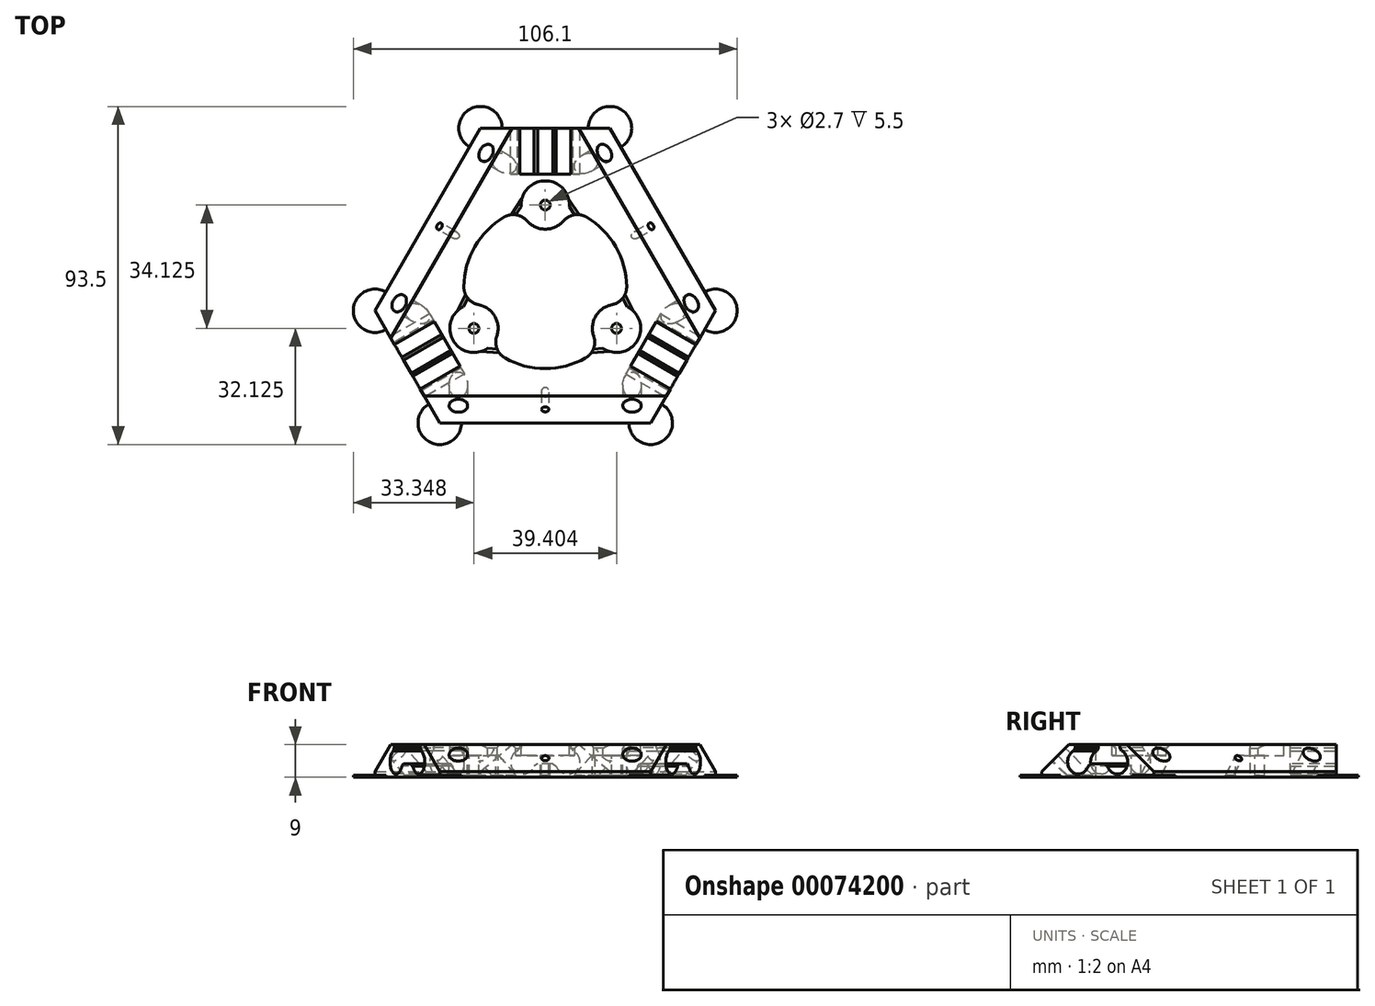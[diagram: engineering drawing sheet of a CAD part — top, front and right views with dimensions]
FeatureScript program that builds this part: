
annotation { "Feature Type Name" : "Feature", "Feature Type Description" : "" }
export const myFeature = defineFeature(function(context is Context, id is Id, definition is map)
    precondition{}
    {
        {
            var Q0;
            Q0=qCreatedBy(makeId("Top.planeOp"),FACE);
            var sketch = newSketch(context, id + "F0", { "sketchPlane" : qUnion([Q0])});
            skCircle(sketch, "E0", {"center": v(0, 0) * mm, "radius": 22.5 * mm, "construction": true});
            skLineSegment(sketch, "E1", {"start": v(0, 0) * mm, "end": v(0, 44) * mm, "construction": true});
            skLineSegment(sketch, "E2", {"start": v(-17.9, 44) * mm, "end": v(17.9, 44) * mm});
            skLineSegment(sketch, "E3", {"start": v(17.9, 44) * mm, "end": v(47.05, -6.5) * mm, "construction": true});
            skLineSegment(sketch, "E4", {"start": v(0, 0) * mm, "end": v(32.48, 18.75) * mm});
            skLineSegment(sketch, "E5.MirrorCS", {"start": v(29.15, -37.5) * mm, "end": v(47.05, -6.5) * mm, "construction": true});
            skLineSegment(sketch, "E6", {"start": v(17.9, 44) * mm, "end": v(32.48, 18.75) * mm});
            skLineSegment(sketch, "E7.MirrorCS", {"start": v(0, 0) * mm, "end": v(-32.48, 18.75) * mm});
            skLineSegment(sketch, "E8.MirrorCS", {"start": v(-17.9, 44) * mm, "end": v(-32.48, 18.75) * mm});
            skSolve(sketch);
        }
        {
            var Q0;
            Q0 = qSketchRegion(id + "F0", true);
            extrude(context, id + "F1", {"entities" : qUnion([Q0]), "depth" : 9 * mm});
        }
        {
            var Q0;
            Q0=makeQuery(id+"F1.opExtrude","CAP_EDGE",EDGE,{"disambiguationData":[OSD([sQuery(id+"F0.wireOp",EDGE,"E8.MirrorCS")])],"isStart":false});
            var Q1;
            Q1=makeQuery(id+"F1.opExtrude","CAP_EDGE",EDGE,{"disambiguationData":[OSD([sQuery(id+"F0.wireOp",EDGE,"E6")])],"isStart":false});
            chamfer(context, id + "F2", {"entities" : qUnion([Q0, Q1]), "width" : 7.5 * mm, "tangentPropagation" : true});
        }
        {
            var Q0;
            Q0=makeQuery(id+"F1.opExtrude","CAP_FACE",FACE,{"disambiguationData":[OSD([sQuery(id+"F0.wireOp",EDGE,"E2"),sQuery(id+"F0.wireOp",EDGE,"E4"),sQuery(id+"F0.wireOp",EDGE,"E6"),sQuery(id+"F0.wireOp",EDGE,"E7.MirrorCS"),sQuery(id+"F0.wireOp",EDGE,"E8.MirrorCS")])],"isStart":false});
            var sketch = newSketch(context, id + "F3", { "sketchPlane" : qUnion([Q0])});
            skCircle(sketch, "E9", {"center": v(0, 0) * mm, "radius": 22.5 * mm});
            skSolve(sketch);
        }
        {
            var Q0;
            Q0 = qSketchRegion(id + "F3", true);
            extrude(context, id + "F4", {"entities" : qUnion([Q0]), "operationType" : NewBodyOperationType.REMOVE, "endBound" : BoundingType.THROUGH_ALL, "oppositeDirection" : true, "depth" : 25 * mm});
        }
        {
            var Q0;
            Q0=makeQuery(id+"F2.opChamfer","BLEND_FACE",FACE,{"disambiguationData":[OSD([sQuery(id+"F0.wireOp",EDGE,"E6")])]});
            var sketch = newSketch(context, id + "F5", { "sketchPlane" : qUnion([Q0])});
            skCircle(sketch, "E10", {"center": v(-0.66, 30.44) * mm, "radius": 2.55 * mm});
            skCircle(sketch, "E11", {"center": v(15.61, 12.75) * mm, "radius": 1 * mm});
            skSolve(sketch);
        }
        {
            var Q0;
            Q0 = qSketchRegion(id + "F5", true);
            extrude(context, id + "F6", {"entities" : qUnion([Q0]), "operationType" : NewBodyOperationType.REMOVE, "endBound" : BoundingType.THROUGH_ALL, "oppositeDirection" : true, "depth" : 25 * mm});
        }
        {
            var Q0;
            Q0=makeQuery(id+"F2.opChamfer","BLEND_FACE",FACE,{"disambiguationData":[OSD([sQuery(id+"F0.wireOp",EDGE,"E8.MirrorCS")])]});
            var sketch = newSketch(context, id + "F7", { "sketchPlane" : qUnion([Q0])});
            skCircle(sketch, "E12", {"center": v(0.66, 30.44) * mm, "radius": 2.55 * mm});
            skCircle(sketch, "E13", {"center": v(-15.61, 12.75) * mm, "radius": 1 * mm});
            skSolve(sketch);
        }
        {
            var Q0;
            Q0 = qSketchRegion(id + "F7", true);
            extrude(context, id + "F8", {"entities" : qUnion([Q0]), "operationType" : NewBodyOperationType.REMOVE, "endBound" : BoundingType.THROUGH_ALL, "oppositeDirection" : true, "depth" : 25 * mm});
        }
        {
            var Q0;
            Q0=makeQuery(id+"F1.opExtrude","SWEPT_FACE",FACE,{"disambiguationData":[OSD([sQuery(id+"F0.wireOp",EDGE,"E2")])]});
            var sketch = newSketch(context, id + "F9", { "sketchPlane" : qUnion([Q0])});
            skLineSegment(sketch, "E14", {"start": v(0, 9) * mm, "end": v(0, 0) * mm, "construction": true});
            skCircle(sketch, "E15", {"center": v(0, 9.46) * mm, "radius": 4.75 * mm, "construction": true});
            skLineSegment(sketch, "E16", {"start": v(0, 9.46) * mm, "end": v(-3.64, 6.4) * mm, "construction": true});
            skCircle(sketch, "E17", {"center": v(-6.22, 4.24) * mm, "radius": 3.38 * mm});
            skLineSegment(sketch, "E18", {"start": v(-9.6, 4.24) * mm, "end": v(-6.22, 4.24) * mm, "construction": true});
            skLineSegment(sketch, "E19", {"start": v(-6.22, 4.24) * mm, "end": v(-7.1, 7.5) * mm, "construction": true});
            skCircle(sketch, "E20.MirrorC", {"center": v(6.22, 4.24) * mm, "radius": 3.38 * mm});
            skSolve(sketch);
        }
        {
            var Q0;
            Q0 = qSketchRegion(id + "F9", true);
            extrude(context, id + "F10", {"entities" : qUnion([Q0]), "operationType" : NewBodyOperationType.REMOVE, "oppositeDirection" : true, "depth" : 12.7 * mm});
        }
        {
            var Q0;
            Q0=makeQuery(id+"F1.opExtrude","SWEPT_FACE",FACE,{"disambiguationData":[OSD([sQuery(id+"F0.wireOp",EDGE,"E2")])]});
            var sketch = newSketch(context, id + "F11", { "sketchPlane" : qUnion([Q0])});
            skLineSegment(sketch, "E21", {"start": v(0, 9) * mm, "end": v(0, 0) * mm, "construction": true});
            skLineSegment(sketch, "E22.bottom", {"start": v(-7.1, 9) * mm, "end": v(7.1, 9) * mm});
            skLineSegment(sketch, "E22.top", {"start": v(-7.1, 3.74) * mm, "end": v(7.1, 3.74) * mm});
            skLineSegment(sketch, "E22.left", {"start": v(-7.1, 9) * mm, "end": v(-7.1, 3.74) * mm});
            skLineSegment(sketch, "E22.right", {"start": v(7.1, 9) * mm, "end": v(7.1, 3.74) * mm});
            skPoint(sketch, "E23", {"position": v(-7.1, 7.5) * mm});
            skLineSegment(sketch, "E24", {"start": v(-6.22, 4.24) * mm, "end": v(6.22, 4.24) * mm, "construction": true});
            skSolve(sketch);
        }
        {
            var Q0;
            Q0 = qSketchRegion(id + "F11", true);
            var Q1;
            Q1=makeQuery(id+"F10.boolean.opBoolean","COPY",FACE,{"derivedFrom":makeQuery(id+"F10.opExtrude","CAP_FACE",FACE,{"disambiguationData":[OSD([sQuery(id+"F9.wireOp",EDGE,"E17")])],"isStart":false})});
            extrude(context, id + "F12", {"entities" : qUnion([Q0]), "operationType" : NewBodyOperationType.REMOVE, "endBound" : BoundingType.UP_TO_SURFACE, "oppositeDirection" : true, "endBoundEntityFace" : qUnion([Q1]), "depth" : 25 * mm});
        }
        {
            var Q0;
            Q0=makeQuery(id+"F1.opExtrude","CAP_FACE",FACE,{"disambiguationData":[OSD([sQuery(id+"F0.wireOp",EDGE,"E2"),sQuery(id+"F0.wireOp",EDGE,"E4"),sQuery(id+"F0.wireOp",EDGE,"E6"),sQuery(id+"F0.wireOp",EDGE,"E7.MirrorCS"),sQuery(id+"F0.wireOp",EDGE,"E8.MirrorCS")])],"isStart":false});
            var sketch = newSketch(context, id + "F13", { "sketchPlane" : qUnion([Q0])});
            skLineSegment(sketch, "E25", {"start": v(0, 0) * mm, "end": v(0, 22.75) * mm, "construction": true});
            skCircle(sketch, "E26", {"center": v(0, 22.75) * mm, "radius": 6.68 * mm});
            skSolve(sketch);
        }
        {
            var Q0;
            Q0 = qSketchRegion(id + "F13", true);
            extrude(context, id + "F14", {"entities" : qUnion([Q0]), "operationType" : NewBodyOperationType.REMOVE, "oppositeDirection" : true, "depth" : 3 * mm});
        }
        {
            var Q0;
            Q0=makeQuery(id+"F14.boolean.opBoolean","COPY",FACE,{"derivedFrom":makeQuery(id+"F14.opExtrude","CAP_FACE",FACE,{"disambiguationData":[OSD([sQuery(id+"F13.wireOp",EDGE,"E26")])],"isStart":false})});
            var sketch = newSketch(context, id + "F15", { "sketchPlane" : qUnion([Q0])});
            skCircle(sketch, "E27", {"center": v(0, 22.75) * mm, "radius": 6.68 * mm});
            skSolve(sketch);
        }
        {
            var Q0;
            Q0 = qSketchRegion(id + "F15", true);
            var Q1;
            Q1=makeQuery(id+"F1.opExtrude","CAP_FACE",FACE,{"disambiguationData":[OSD([sQuery(id+"F0.wireOp",EDGE,"E2"),sQuery(id+"F0.wireOp",EDGE,"E4"),sQuery(id+"F0.wireOp",EDGE,"E6"),sQuery(id+"F0.wireOp",EDGE,"E7.MirrorCS"),sQuery(id+"F0.wireOp",EDGE,"E8.MirrorCS")])],"isStart":true});
            extrude(context, id + "F16", {"entities" : qUnion([Q0]), "operationType" : NewBodyOperationType.ADD, "endBound" : BoundingType.UP_TO_SURFACE, "oppositeDirection" : true, "endBoundEntityFace" : qUnion([Q1]), "depth" : 25 * mm});
        }
        {
            var Q0;
            Q0=makeQuery(id+"F16.boolean.opBoolean","MERGE",FACE,{"derivedFrom":[makeQuery(id+"F14.boolean.opBoolean","COPY",FACE,{"derivedFrom":makeQuery(id+"F14.opExtrude","CAP_FACE",FACE,{"disambiguationData":[OSD([sQuery(id+"F13.wireOp",EDGE,"E26")])],"isStart":false})}),makeQuery(id+"F16.opExtrude","CAP_FACE",FACE,{"disambiguationData":[OSD([sQuery(id+"F15.wireOp",EDGE,"E27")])],"isStart":true})]});
            var sketch = newSketch(context, id + "F17", { "sketchPlane" : qUnion([Q0])});
            skCircle(sketch, "E28", {"center": v(0, 22.75) * mm, "radius": 1.35 * mm});
            skSolve(sketch);
        }
        {
            var Q0;
            Q0 = qSketchRegion(id + "F17", true);
            extrude(context, id + "F18", {"entities" : qUnion([Q0]), "operationType" : NewBodyOperationType.REMOVE, "endBound" : BoundingType.THROUGH_ALL, "oppositeDirection" : true, "depth" : 25 * mm});
        }
        {
            var Q0;
            Q0=makeQuery(id+"F12.boolean.opBoolean","INTERSECT",EDGE,{"derivedFrom":[makeQuery(id+"F10.boolean.opBoolean","COPY",FACE,{"derivedFrom":makeQuery(id+"F10.opExtrude","SWEPT_FACE",FACE,{"disambiguationData":[OSD([sQuery(id+"F9.wireOp",EDGE,"E17")])]})}),makeQuery(id+"F12.opExtrude","SWEPT_FACE",FACE,{"disambiguationData":[OSD([sQuery(id+"F11.wireOp",EDGE,"E22.left")])]})]});
            var Q1;
            Q1=makeQuery(id+"F12.boolean.opBoolean","INTERSECT",EDGE,{"derivedFrom":[makeQuery(id+"F10.boolean.opBoolean","COPY",FACE,{"derivedFrom":makeQuery(id+"F10.opExtrude","SWEPT_FACE",FACE,{"disambiguationData":[OSD([sQuery(id+"F9.wireOp",EDGE,"E20.MirrorC")])]})}),makeQuery(id+"F12.opExtrude","SWEPT_FACE",FACE,{"disambiguationData":[OSD([sQuery(id+"F11.wireOp",EDGE,"E22.right")])]})]});
            var Q2;
            Q2=makeQuery(id+"F14.boolean.opBoolean","INTERSECT",EDGE,{"disambiguationData":[OD(1.0)],"derivedFrom":[makeQuery(id+"F4.boolean.opBoolean","COPY",FACE,{"derivedFrom":makeQuery(id+"F4.opExtrude","SWEPT_FACE",FACE,{"disambiguationData":[OSD([sQuery(id+"F3.wireOp",EDGE,"E9")])]})}),makeQuery(id+"F14.opExtrude","SWEPT_FACE",FACE,{"disambiguationData":[OSD([sQuery(id+"F13.wireOp",EDGE,"E26")])]})]});
            var Q3;
            Q3=makeQuery(id+"F14.boolean.opBoolean","INTERSECT",EDGE,{"disambiguationData":[OD(0.0)],"derivedFrom":[makeQuery(id+"F4.boolean.opBoolean","COPY",FACE,{"derivedFrom":makeQuery(id+"F4.opExtrude","SWEPT_FACE",FACE,{"disambiguationData":[OSD([sQuery(id+"F3.wireOp",EDGE,"E9")])]})}),makeQuery(id+"F14.opExtrude","SWEPT_FACE",FACE,{"disambiguationData":[OSD([sQuery(id+"F13.wireOp",EDGE,"E26")])]})]});
            var Q4;
            Q4=makeQuery(id+"F12.boolean.opBoolean","INTERSECT",EDGE,{"derivedFrom":[makeQuery(id+"F10.boolean.opBoolean","COPY",FACE,{"derivedFrom":makeQuery(id+"F10.opExtrude","SWEPT_FACE",FACE,{"disambiguationData":[OSD([sQuery(id+"F9.wireOp",EDGE,"E17")])]})}),makeQuery(id+"F12.opExtrude","SWEPT_FACE",FACE,{"disambiguationData":[OSD([sQuery(id+"F11.wireOp",EDGE,"E22.top")])]})]});
            var Q5;
            Q5=makeQuery(id+"F12.boolean.opBoolean","INTERSECT",EDGE,{"derivedFrom":[makeQuery(id+"F10.boolean.opBoolean","COPY",FACE,{"derivedFrom":makeQuery(id+"F10.opExtrude","SWEPT_FACE",FACE,{"disambiguationData":[OSD([sQuery(id+"F9.wireOp",EDGE,"E20.MirrorC")])]})}),makeQuery(id+"F12.opExtrude","SWEPT_FACE",FACE,{"disambiguationData":[OSD([sQuery(id+"F11.wireOp",EDGE,"E22.top")])]})]});
            var Q6;
            Q6=makeQuery(id+"F6.boolean.opBoolean","COPY",EDGE,{"derivedFrom":makeQuery(id+"F6.opExtrude","CAP_EDGE",EDGE,{"disambiguationData":[OSD([sQuery(id+"F5.wireOp",EDGE,"E11")])],"isStart":true})});
            var Q7;
            Q7=makeQuery(id+"F8.boolean.opBoolean","COPY",EDGE,{"derivedFrom":makeQuery(id+"F8.opExtrude","CAP_EDGE",EDGE,{"disambiguationData":[OSD([sQuery(id+"F7.wireOp",EDGE,"E13")])],"isStart":true})});
            chamfer(context, id + "F19", {"entities" : qUnion([Q0, Q1, Q2, Q3, Q4, Q5, Q6, Q7]), "width" : 1 * mm, "tangentPropagation" : true});
        }
        {
            var Q0;
            Q0=makeQuery(id+"F16.boolean.opBoolean","INTERSECT",EDGE,{"disambiguationData":[OD(1.0)],"derivedFrom":[makeQuery(id+"F4.boolean.opBoolean","COPY",FACE,{"derivedFrom":makeQuery(id+"F4.opExtrude","SWEPT_FACE",FACE,{"disambiguationData":[OSD([sQuery(id+"F3.wireOp",EDGE,"E9")])]})}),makeQuery(id+"F16.opExtrude","SWEPT_FACE",FACE,{"disambiguationData":[OSD([sQuery(id+"F15.wireOp",EDGE,"E27")])]})]});
            var Q1;
            Q1=makeQuery(id+"F16.boolean.opBoolean","INTERSECT",EDGE,{"disambiguationData":[OD(0.0)],"derivedFrom":[makeQuery(id+"F4.boolean.opBoolean","COPY",FACE,{"derivedFrom":makeQuery(id+"F4.opExtrude","SWEPT_FACE",FACE,{"disambiguationData":[OSD([sQuery(id+"F3.wireOp",EDGE,"E9")])]})}),makeQuery(id+"F16.opExtrude","SWEPT_FACE",FACE,{"disambiguationData":[OSD([sQuery(id+"F15.wireOp",EDGE,"E27")])]})]});
            fillet(context, id + "F20", {"entities" : qUnion([Q0, Q1]), "radius" : 5 * mm, "tangentPropagation" : true, "allowEdgeOverflow" : false});
        }
        {
            var Q0;
            {var subQ0=sQuery(id+"F0.wireOp",EDGE,"E7.MirrorCS");var subQ1=sQuery(id+"F3.wireOp",EDGE,"E9");Q0=makeQuery(id+"F14.boolean.opBoolean","SPLIT",EDGE,{"disambiguationData":[TD([makeQuery(id+"F1.opExtrude","SWEPT_FACE",FACE,{"disambiguationData":[OSD([subQ0])]})])],"derivedFrom":makeQuery(id+"F4.boolean.opBoolean","COPY",EDGE,{"derivedFrom":makeQuery(id+"F4.opExtrude","CAP_EDGE",EDGE,{"disambiguationData":[OSD([subQ1])],"isStart":true})})});}
            var Q1;
            {var subQ0=sQuery(id+"F0.wireOp",EDGE,"E4");var subQ1=sQuery(id+"F3.wireOp",EDGE,"E9");Q1=makeQuery(id+"F14.boolean.opBoolean","SPLIT",EDGE,{"disambiguationData":[TD([makeQuery(id+"F1.opExtrude","SWEPT_FACE",FACE,{"disambiguationData":[OSD([subQ0])]})])],"derivedFrom":makeQuery(id+"F4.boolean.opBoolean","COPY",EDGE,{"derivedFrom":makeQuery(id+"F4.opExtrude","CAP_EDGE",EDGE,{"disambiguationData":[OSD([subQ1])],"isStart":true})})});}
            var Q2;
            Q2=makeQuery(id+"F19.opChamfer","BLEND_EDGE",EDGE,{"blendedFrom":[makeQuery(id+"F14.boolean.opBoolean","INTERSECT",EDGE,{"disambiguationData":[OD(1.0)],"derivedFrom":[makeQuery(id+"F4.boolean.opBoolean","COPY",FACE,{"derivedFrom":makeQuery(id+"F4.opExtrude","SWEPT_FACE",FACE,{"disambiguationData":[OSD([sQuery(id+"F3.wireOp",EDGE,"E9")])]})}),makeQuery(id+"F14.opExtrude","SWEPT_FACE",FACE,{"disambiguationData":[OSD([sQuery(id+"F13.wireOp",EDGE,"E26")])]})]}),makeQuery(id+"F1.opExtrude","CAP_FACE",FACE,{"disambiguationData":[OSD([sQuery(id+"F0.wireOp",EDGE,"E2"),sQuery(id+"F0.wireOp",EDGE,"E4"),sQuery(id+"F0.wireOp",EDGE,"E6"),sQuery(id+"F0.wireOp",EDGE,"E7.MirrorCS"),sQuery(id+"F0.wireOp",EDGE,"E8.MirrorCS")])],"isStart":false})],"blendedInto":[makeQuery(id+"F1.opExtrude","CAP_FACE",FACE,{"disambiguationData":[OSD([sQuery(id+"F0.wireOp",EDGE,"E2"),sQuery(id+"F0.wireOp",EDGE,"E4"),sQuery(id+"F0.wireOp",EDGE,"E6"),sQuery(id+"F0.wireOp",EDGE,"E7.MirrorCS"),sQuery(id+"F0.wireOp",EDGE,"E8.MirrorCS")])],"isStart":false})]});
            var Q3;
            Q3=makeQuery(id+"F19.opChamfer","BLEND_EDGE",EDGE,{"blendedFrom":[makeQuery(id+"F14.boolean.opBoolean","INTERSECT",EDGE,{"disambiguationData":[OD(0.0)],"derivedFrom":[makeQuery(id+"F4.boolean.opBoolean","COPY",FACE,{"derivedFrom":makeQuery(id+"F4.opExtrude","SWEPT_FACE",FACE,{"disambiguationData":[OSD([sQuery(id+"F3.wireOp",EDGE,"E9")])]})}),makeQuery(id+"F14.opExtrude","SWEPT_FACE",FACE,{"disambiguationData":[OSD([sQuery(id+"F13.wireOp",EDGE,"E26")])]})]}),makeQuery(id+"F1.opExtrude","CAP_FACE",FACE,{"disambiguationData":[OSD([sQuery(id+"F0.wireOp",EDGE,"E2"),sQuery(id+"F0.wireOp",EDGE,"E4"),sQuery(id+"F0.wireOp",EDGE,"E6"),sQuery(id+"F0.wireOp",EDGE,"E7.MirrorCS"),sQuery(id+"F0.wireOp",EDGE,"E8.MirrorCS")])],"isStart":false})],"blendedInto":[makeQuery(id+"F1.opExtrude","CAP_FACE",FACE,{"disambiguationData":[OSD([sQuery(id+"F0.wireOp",EDGE,"E2"),sQuery(id+"F0.wireOp",EDGE,"E4"),sQuery(id+"F0.wireOp",EDGE,"E6"),sQuery(id+"F0.wireOp",EDGE,"E7.MirrorCS"),sQuery(id+"F0.wireOp",EDGE,"E8.MirrorCS")])],"isStart":false})]});
            chamfer(context, id + "F21", {"entities" : qUnion([Q0, Q1, Q2, Q3]), "width" : 1 * mm, "tangentPropagation" : true});
        }
        {
            var Q0;
            Q0=makeQuery(id+"F1.opExtrude","SWEPT_BODY",BODY,{"disambiguationData":[OSD([sQuery(id+"F0.wireOp",EDGE,"E2"),sQuery(id+"F0.wireOp",EDGE,"E4"),sQuery(id+"F0.wireOp",EDGE,"E6"),sQuery(id+"F0.wireOp",EDGE,"E7.MirrorCS"),sQuery(id+"F0.wireOp",EDGE,"E8.MirrorCS")])]});
            var Q1;
            {var subQ0=sQuery(id+"F0.wireOp",EDGE,"E7.MirrorCS");Q1=makeQuery(id+"F16.boolean.opBoolean","SPLIT",FACE,{"disambiguationData":[TD([makeQuery(id+"F1.opExtrude","SWEPT_FACE",FACE,{"disambiguationData":[OSD([subQ0])]})])],"derivedFrom":makeQuery(id+"F4.boolean.opBoolean","COPY",FACE,{"derivedFrom":makeQuery(id+"F4.opExtrude","SWEPT_FACE",FACE,{"disambiguationData":[OSD([sQuery(id+"F3.wireOp",EDGE,"E9")])]})})});}
            circularPattern(context, id + "F22", {"entities" : qUnion([Q0]), "axis" : qUnion([Q1]), "angle" : 120 * degree, "instanceCount" : 3});
        }
        {
            var Q0;
            Q0=makeQuery(id+"F1.opExtrude","SWEPT_BODY",BODY,{"disambiguationData":[OSD([sQuery(id+"F0.wireOp",EDGE,"E2"),sQuery(id+"F0.wireOp",EDGE,"E4"),sQuery(id+"F0.wireOp",EDGE,"E6"),sQuery(id+"F0.wireOp",EDGE,"E7.MirrorCS"),sQuery(id+"F0.wireOp",EDGE,"E8.MirrorCS")])]});
            var Q1;
            Q1=makeQuery(id+"F22.opPattern","COPY",BODY,{"derivedFrom":makeQuery(id+"F1.opExtrude","SWEPT_BODY",BODY,{"disambiguationData":[OSD([sQuery(id+"F0.wireOp",EDGE,"E2"),sQuery(id+"F0.wireOp",EDGE,"E4"),sQuery(id+"F0.wireOp",EDGE,"E6"),sQuery(id+"F0.wireOp",EDGE,"E7.MirrorCS"),sQuery(id+"F0.wireOp",EDGE,"E8.MirrorCS")])]}),"instanceName":"1"});
            var Q2;
            Q2=makeQuery(id+"F22.opPattern","COPY",BODY,{"derivedFrom":makeQuery(id+"F1.opExtrude","SWEPT_BODY",BODY,{"disambiguationData":[OSD([sQuery(id+"F0.wireOp",EDGE,"E2"),sQuery(id+"F0.wireOp",EDGE,"E4"),sQuery(id+"F0.wireOp",EDGE,"E6"),sQuery(id+"F0.wireOp",EDGE,"E7.MirrorCS"),sQuery(id+"F0.wireOp",EDGE,"E8.MirrorCS")])]}),"instanceName":"2"});
            booleanBodies(context, id + "F23", {"operationType" : BooleanOperationType.UNION, "tools" : qUnion([Q0, Q1, Q2])});
        }
        {
            var Q0;
            {var subQ0=makeQuery(id+"F16.boolean.opBoolean","MERGE",FACE,{"derivedFrom":[makeQuery(id+"F1.opExtrude","CAP_FACE",FACE,{"disambiguationData":[OSD([sQuery(id+"F0.wireOp",EDGE,"E2"),sQuery(id+"F0.wireOp",EDGE,"E4"),sQuery(id+"F0.wireOp",EDGE,"E6"),sQuery(id+"F0.wireOp",EDGE,"E7.MirrorCS"),sQuery(id+"F0.wireOp",EDGE,"E8.MirrorCS")])],"isStart":true}),makeQuery(id+"F16.opExtrude","CAP_FACE",FACE,{"disambiguationData":[OSD([sQuery(id+"F15.wireOp",EDGE,"E27")])],"isStart":false})]});Q0=makeQuery(id+"F23.opBoolean","MERGE",FACE,{"derivedFrom":[subQ0,makeQuery(id+"F22.opPattern","COPY",FACE,{"derivedFrom":subQ0,"instanceName":"1"}),makeQuery(id+"F22.opPattern","COPY",FACE,{"derivedFrom":subQ0,"instanceName":"2"})]});}
            var sketch = newSketch(context, id + "F24", { "sketchPlane" : qUnion([Q0])});
            skLineSegment(sketch, "E29.0", {"start": v(47.05, 6.5) * mm, "end": v(29.16, 37.5) * mm});
            skLineSegment(sketch, "E29.1", {"start": v(-29.15, 37.5) * mm, "end": v(-47.05, 6.5) * mm});
            skLineSegment(sketch, "E29.2", {"start": v(-17.9, -44) * mm, "end": v(17.9, -44) * mm});
            skLineSegment(sketch, "E30", {"start": v(-29.15, 37.5) * mm, "end": v(29.16, 37.5) * mm});
            skLineSegment(sketch, "E31", {"start": v(47.05, 6.5) * mm, "end": v(17.9, -44) * mm});
            skLineSegment(sketch, "E32", {"start": v(-47.05, 6.5) * mm, "end": v(-17.9, -44) * mm});
            skArc(sketch, "E33.0", {"start": v(13.4, 13.56) * mm, "mid": v(13.92, 8.04) * mm, "end": v(18.44, 4.82) * mm});
            skArc(sketch, "E33.1", {"start": v(11.15, 19.54) * mm, "mid": v(13.35, 16.96) * mm, "end": v(13.4, 13.56) * mm});
            skArc(sketch, "E33.2", {"start": v(18.44, 4.82) * mm, "mid": v(21.36, 3.08) * mm, "end": v(22.5, -0.12) * mm});
            skArc(sketch, "E33.3", {"start": v(11.35, -19.43) * mm, "mid": v(8.01, -20.04) * mm, "end": v(5.05, -18.38) * mm});
            skArc(sketch, "E33.4", {"start": v(5.05, -18.38) * mm, "mid": v(0, -16.07) * mm, "end": v(-5.05, -18.38) * mm});
            skArc(sketch, "E33.5", {"start": v(-5.05, -18.38) * mm, "mid": v(-8.01, -20.04) * mm, "end": v(-11.35, -19.43) * mm});
            skArc(sketch, "E33.6", {"start": v(-13.4, 13.56) * mm, "mid": v(-13.35, 16.96) * mm, "end": v(-11.15, 19.54) * mm});
            skArc(sketch, "E33.7", {"start": v(-18.44, 4.82) * mm, "mid": v(-13.92, 8.04) * mm, "end": v(-13.4, 13.56) * mm});
            skArc(sketch, "E33.8", {"start": v(-22.5, -0.12) * mm, "mid": v(-21.36, 3.08) * mm, "end": v(-18.44, 4.82) * mm});
            skArc(sketch, "E34", {"start": v(11.15, 19.54) * mm, "mid": v(0, 22.5) * mm, "end": v(-11.15, 19.54) * mm});
            skArc(sketch, "E35.trimOffspring", {"start": v(-22.5, -0.12) * mm, "mid": v(-19.49, -11.25) * mm, "end": v(-11.35, -19.43) * mm});
            skArc(sketch, "E36.trimOffspring", {"start": v(11.35, -19.43) * mm, "mid": v(19.49, -11.25) * mm, "end": v(22.5, -0.12) * mm});
            skSolve(sketch);
        }
        {
            var Q0;
            Q0 = qSketchRegion(id + "F24", true);
            extrude(context, id + "F25", {"entities" : qUnion([Q0]), "operationType" : NewBodyOperationType.ADD, "oppositeDirection" : true, "depth" : 0.5 * mm});
        }
        {
            var Q0;
            {var subQ0=makeQuery(id+"F16.boolean.opBoolean","MERGE",FACE,{"derivedFrom":[makeQuery(id+"F1.opExtrude","CAP_FACE",FACE,{"disambiguationData":[OSD([sQuery(id+"F0.wireOp",EDGE,"E2"),sQuery(id+"F0.wireOp",EDGE,"E4"),sQuery(id+"F0.wireOp",EDGE,"E6"),sQuery(id+"F0.wireOp",EDGE,"E7.MirrorCS"),sQuery(id+"F0.wireOp",EDGE,"E8.MirrorCS")])],"isStart":true}),makeQuery(id+"F16.opExtrude","CAP_FACE",FACE,{"disambiguationData":[OSD([sQuery(id+"F15.wireOp",EDGE,"E27")])],"isStart":false})]});Q0=makeQuery(id+"F25.boolean.opBoolean","MERGE",FACE,{"derivedFrom":[makeQuery(id+"F23.opBoolean","MERGE",FACE,{"derivedFrom":[subQ0,makeQuery(id+"F22.opPattern","COPY",FACE,{"derivedFrom":subQ0,"instanceName":"1"}),makeQuery(id+"F22.opPattern","COPY",FACE,{"derivedFrom":subQ0,"instanceName":"2"})]}),makeQuery(id+"F25.opExtrude","CAP_FACE",FACE,{"disambiguationData":[OSD([sQuery(id+"F24.wireOp",EDGE,"E29.0"),sQuery(id+"F24.wireOp",EDGE,"E29.1"),sQuery(id+"F24.wireOp",EDGE,"E29.2"),sQuery(id+"F24.wireOp",EDGE,"E30"),sQuery(id+"F24.wireOp",EDGE,"E31"),sQuery(id+"F24.wireOp",EDGE,"E32"),sQuery(id+"F24.wireOp",EDGE,"E33.0"),sQuery(id+"F24.wireOp",EDGE,"E33.1"),sQuery(id+"F24.wireOp",EDGE,"E33.2"),sQuery(id+"F24.wireOp",EDGE,"E33.3"),sQuery(id+"F24.wireOp",EDGE,"E33.4"),sQuery(id+"F24.wireOp",EDGE,"E33.5"),sQuery(id+"F24.wireOp",EDGE,"E33.6"),sQuery(id+"F24.wireOp",EDGE,"E33.7"),sQuery(id+"F24.wireOp",EDGE,"E33.8"),sQuery(id+"F24.wireOp",EDGE,"E34"),sQuery(id+"F24.wireOp",EDGE,"E35.trimOffspring"),sQuery(id+"F24.wireOp",EDGE,"E36.trimOffspring")])],"isStart":true})]});}
            var sketch = newSketch(context, id + "F26", { "sketchPlane" : qUnion([Q0])});
            skCircle(sketch, "E37", {"center": v(-47.05, 6.5) * mm, "radius": 6 * mm});
            skCircle(sketch, "E38", {"center": v(-29.15, 37.5) * mm, "radius": 6 * mm});
            skCircle(sketch, "E39", {"center": v(29.16, 37.5) * mm, "radius": 6 * mm});
            skCircle(sketch, "E40", {"center": v(47.05, 6.5) * mm, "radius": 6 * mm});
            skCircle(sketch, "E41", {"center": v(17.9, -44) * mm, "radius": 6 * mm});
            skCircle(sketch, "E42", {"center": v(-17.9, -44) * mm, "radius": 6 * mm});
            skSolve(sketch);
        }
        {
            var Q0;
            Q0 = qSketchRegion(id + "F26", true);
            extrude(context, id + "F27", {"entities" : qUnion([Q0]), "operationType" : NewBodyOperationType.ADD, "oppositeDirection" : true, "depth" : 0.5 * mm});
        }
    });
